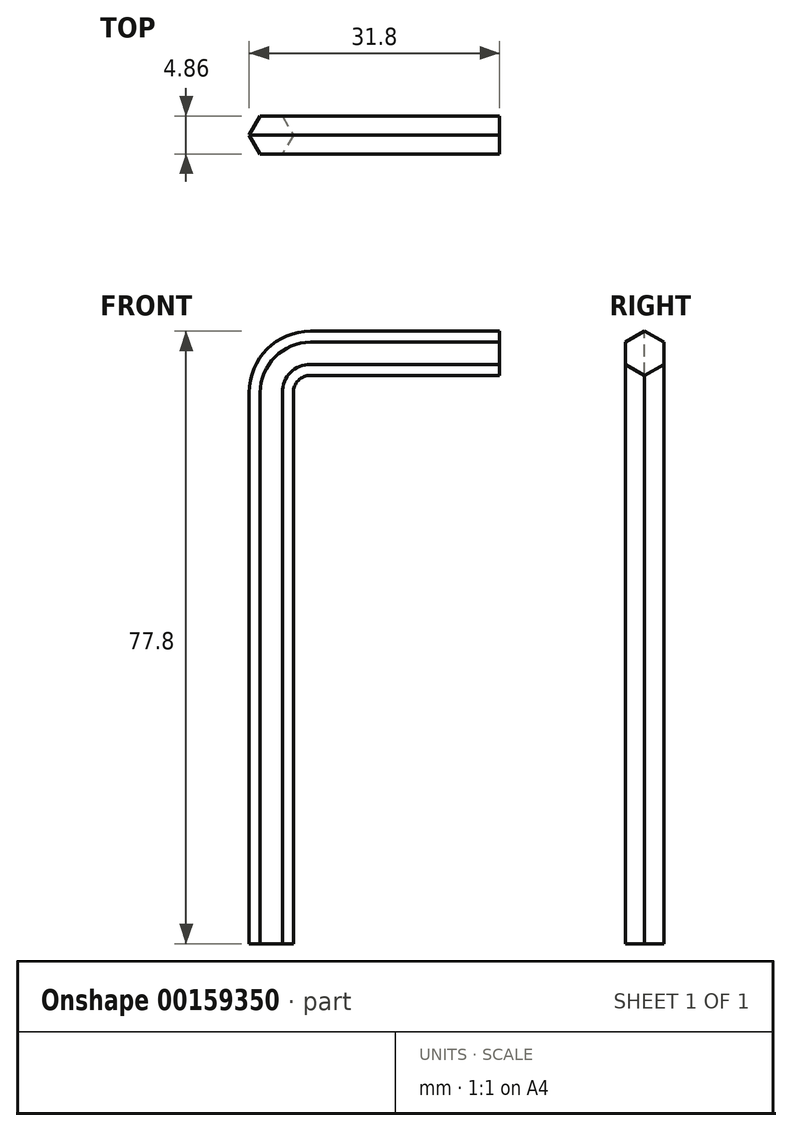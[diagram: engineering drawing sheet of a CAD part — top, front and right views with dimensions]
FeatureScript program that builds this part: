
annotation { "Feature Type Name" : "Feature", "Feature Type Description" : "" }
export const myFeature = defineFeature(function(context is Context, id is Id, definition is map)
    precondition{}
    {
        {
            var Q0;
            Q0=qCreatedBy(makeId("Top.planeOp"),FACE);
            var sketch = newSketch(context, id + "F0", { "sketchPlane" : qUnion([Q0])});
            skCircle(sketch, "E0.cCircle", {"center": v(0, 0) * mm, "radius": 2.43 * mm, "construction": true});
            skLineSegment(sketch, "E0.0", {"start": v(-2.8, 0) * mm, "end": v(-1.4, 2.43) * mm});
            skLineSegment(sketch, "E0.1", {"start": v(-1.4, 2.42) * mm, "end": v(1.4, 2.43) * mm});
            skLineSegment(sketch, "E0.2", {"start": v(1.4, 2.42) * mm, "end": v(2.8, 0) * mm});
            skLineSegment(sketch, "E0.3", {"start": v(2.8, 0) * mm, "end": v(1.4, -2.43) * mm});
            skLineSegment(sketch, "E0.4", {"start": v(1.4, -2.42) * mm, "end": v(-1.4, -2.43) * mm});
            skLineSegment(sketch, "E0.5", {"start": v(-1.4, -2.42) * mm, "end": v(-2.8, 0) * mm});
            skPoint(sketch, "E0.0.midPoint", {"position": v(-2.1, 1.21) * mm});
            skSolve(sketch);
        }
        {
            var Q0;
            Q0=qCreatedBy(makeId("Front.planeOp"),FACE);
            var sketch = newSketch(context, id + "F1", { "sketchPlane" : qUnion([Q0])});
            skLineSegment(sketch, "E1", {"start": v(0, 0) * mm, "end": v(0, 70) * mm});
            skArc(sketch, "E2", {"start": v(5, 75) * mm, "mid": v(1.46, 73.54) * mm, "end": v(0, 70) * mm});
            skLineSegment(sketch, "E3", {"start": v(5, 75) * mm, "end": v(29, 75) * mm});
            skSolve(sketch);
        }
        {
            var Q0;
            Q0=makeQuery(id+"F0.imprint","IMPRINT",FACE,{"disambiguationData":[TD([[makeQuery(id+"F0.imprint","IMPRINT",EDGE,{"derivedFrom":sQuery(id+"F0.wireOp",EDGE,"E0.0")}),-1.0]])]});
            var Q1;
            Q1=sQuery(id+"F1.wireOp",EDGE,"E1");
            var Q2;
            Q2=sQuery(id+"F1.wireOp",EDGE,"E2");
            var Q3;
            Q3=sQuery(id+"F1.wireOp",EDGE,"E3");
            sweep(context, id + "F2", {"profiles" : qUnion([Q0]), "path" : qUnion([Q1, Q2, Q3])});
        }
    });
